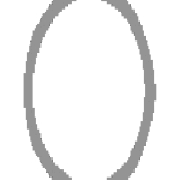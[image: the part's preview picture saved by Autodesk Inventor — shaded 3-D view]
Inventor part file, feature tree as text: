
AUTODESK INVENTOR PART (.ipt)
format: ipt  version: 2021 (Build 250183000, 183)  size: 125,952 bytes
history: native  units: in
note: dims shown in document units (in); Inventor stores cm internally (conversion verified against a paired STEP export)
features: other x4, plane x4, sketch x4, extrude x1, boolean_combine x1
ambient origin geometry x8: Origin, YZ Plane, XZ Plane, XY Plane, X Axis, Y Axis, Z Axis, Center Point
bodies: Solid1 (feature_tree), Body (feature_tree), Solid2 (feature_tree)
feature tree (14):
  other  "Driven Length"
  other  "Frame Generator"
  other  "Start Plane"
  other  "End Plane"
  plane  "Work Plane4"
  plane  "Work Plane5"
  plane  "Work Plane6"
  extrude  "Extrusion3"  Depth=0.065in
  boolean_combine  "Combine1"
  sketch  "Sketch"  dims[d5=13.5in d6=0.12in d7=0.0in d8=90.0deg d9=13.5in d10=0.12in d11=0.0in]
  sketch  "Sketch2"  dims[d0=1.0in d1=0.065in]
  plane  "Work Plane3"
  sketch  "Sketch3"  dims[d2=13.5in]
  sketch  "Sketch4"  dims[d4=-0.0in]
